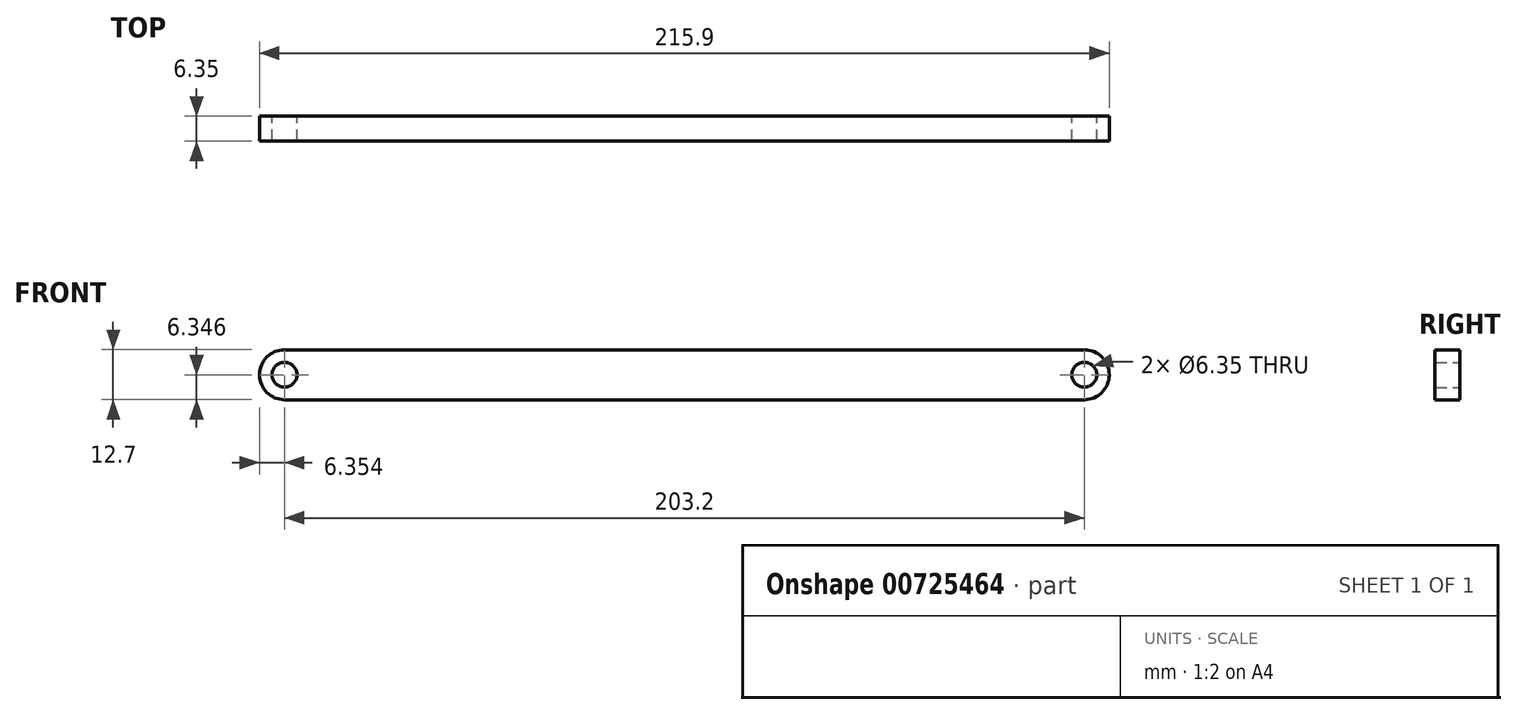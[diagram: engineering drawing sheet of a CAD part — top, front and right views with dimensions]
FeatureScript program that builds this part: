
annotation { "Feature Type Name" : "Feature", "Feature Type Description" : "" }
export const myFeature = defineFeature(function(context is Context, id is Id, definition is map)
    precondition{}
    {
        {
            var Q0;
            Q0=qCreatedBy(makeId("Front.planeOp"),FACE);
            var sketch = newSketch(context, id + "F0", { "sketchPlane" : qUnion([Q0])});
            skLineSegment(sketch, "E0.bottom", {"start": v(-23.84, 6.2) * mm, "end": v(179.36, 6.2) * mm});
            skLineSegment(sketch, "E0.top", {"start": v(-23.84, -6.5) * mm, "end": v(179.36, -6.5) * mm});
            skArc(sketch, "E1", {"start": v(-23.84, -6.5) * mm, "mid": v(-30.19, -0.15) * mm, "end": v(-23.84, 6.2) * mm});
            skArc(sketch, "E2", {"start": v(179.36, -6.5) * mm, "mid": v(185.71, -0.15) * mm, "end": v(179.36, 6.2) * mm});
            skCircle(sketch, "E3", {"center": v(179.36, -0.15) * mm, "radius": 3.18 * mm});
            skCircle(sketch, "E4", {"center": v(-23.84, -0.15) * mm, "radius": 3.18 * mm});
            skSolve(sketch);
        }
        {
            var Q0;
            Q0=makeQuery(id+"F0.imprint","IMPRINT",FACE,{"disambiguationData":[TD([[makeQuery(id+"F0.imprint","IMPRINT",EDGE,{"derivedFrom":sQuery(id+"F0.wireOp",EDGE,"E0.bottom")}),-1.0]])]});
            extrude(context, id + "F1", {"entities" : qUnion([Q0]), "depth" : 6.35 * mm, "offsetDistance" : 25.4 * mm});
        }
    });
